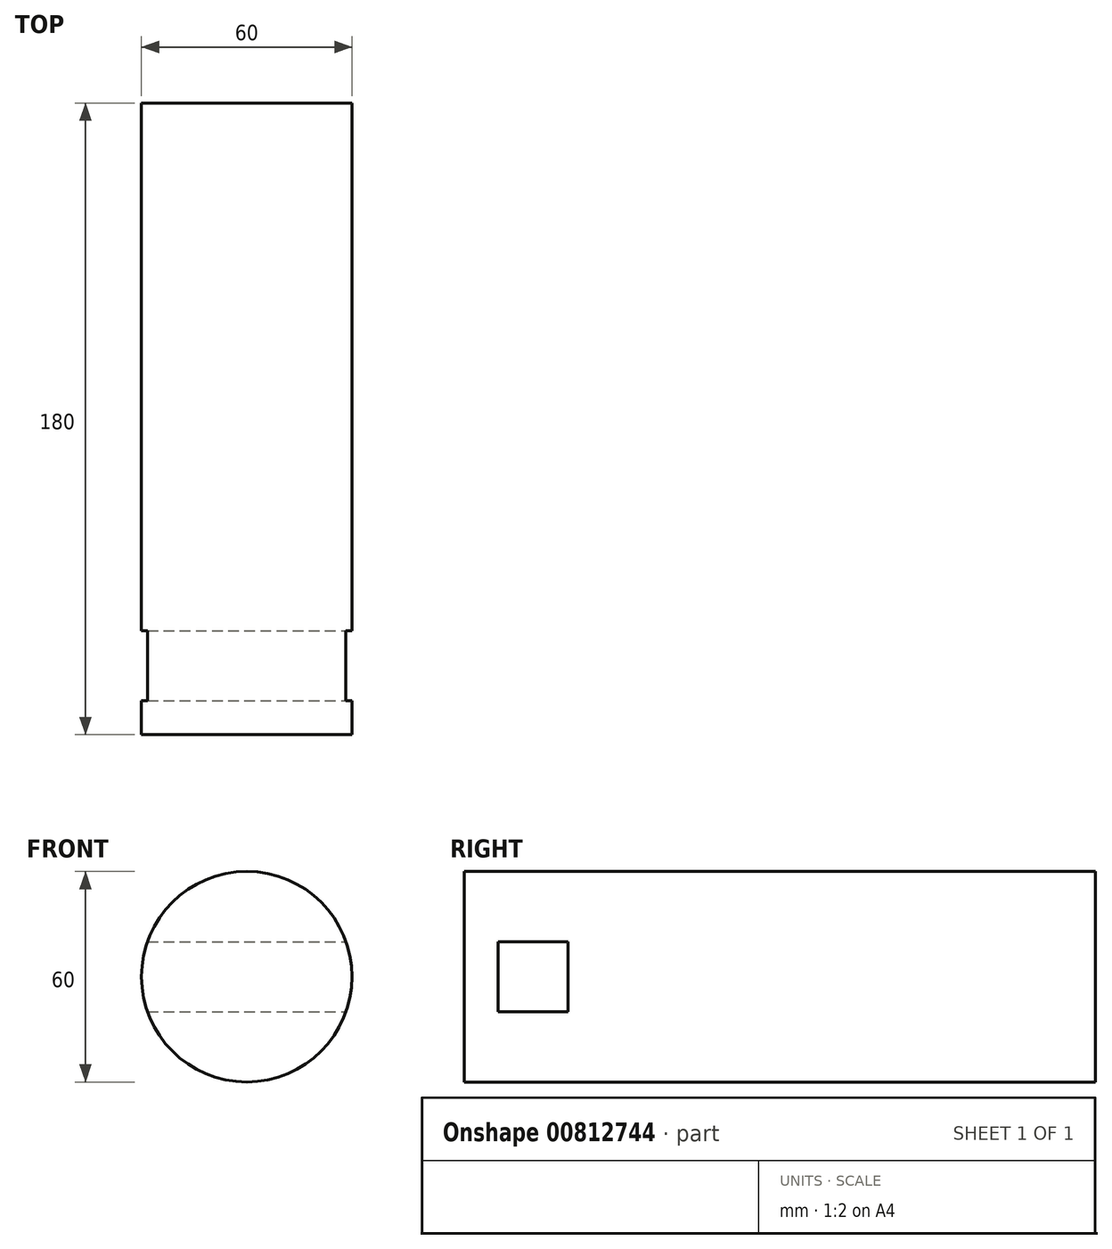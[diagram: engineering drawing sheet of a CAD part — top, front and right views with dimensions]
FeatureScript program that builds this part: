
annotation { "Feature Type Name" : "Feature", "Feature Type Description" : "" }
export const myFeature = defineFeature(function(context is Context, id is Id, definition is map)
    precondition{}
    {
        {
            var Q0;
            Q0=qCreatedBy(makeId("Front.planeOp"),FACE);
            var sketch = newSketch(context, id + "F0", { "sketchPlane" : qUnion([Q0])});
            skCircle(sketch, "E0", {"center": v(0, 0) * mm, "radius": 30 * mm});
            skSolve(sketch);
        }
        {
            var Q0;
            Q0 = qSketchRegion(id + "F0", true);
            extrude(context, id + "F1", {"entities" : qUnion([Q0]), "depth" : 180 * mm, "offsetDistance" : 25 * mm});
        }
        {
            var Q0;
            Q0=qCreatedBy(makeId("Right.planeOp"),FACE);
            var sketch = newSketch(context, id + "F2", { "sketchPlane" : qUnion([Q0])});
            skLineSegment(sketch, "E1.bottom", {"start": v(-170.38, -10) * mm, "end": v(-150.38, -10) * mm});
            skLineSegment(sketch, "E1.top", {"start": v(-170.38, 10) * mm, "end": v(-150.38, 10) * mm});
            skLineSegment(sketch, "E1.left", {"start": v(-170.38, -10) * mm, "end": v(-170.38, 10) * mm});
            skLineSegment(sketch, "E1.right", {"start": v(-150.38, -10) * mm, "end": v(-150.38, 10) * mm});
            skPoint(sketch, "E1.middle", {"position": v(-160.38, 0) * mm});
            skSolve(sketch);
        }
        {
            var Q0;
            Q0 = qSketchRegion(id + "F2", true);
            extrude(context, id + "F3", {"entities" : qUnion([Q0]), "operationType" : NewBodyOperationType.REMOVE, "oppositeDirection" : true, "depth" : 52 * mm, "offsetDistance" : 25 * mm, "hasSecondDirection" : true, "secondDirectionOppositeDirection" : false, "secondDirectionDepth" : 50 * mm});
        }
    });
